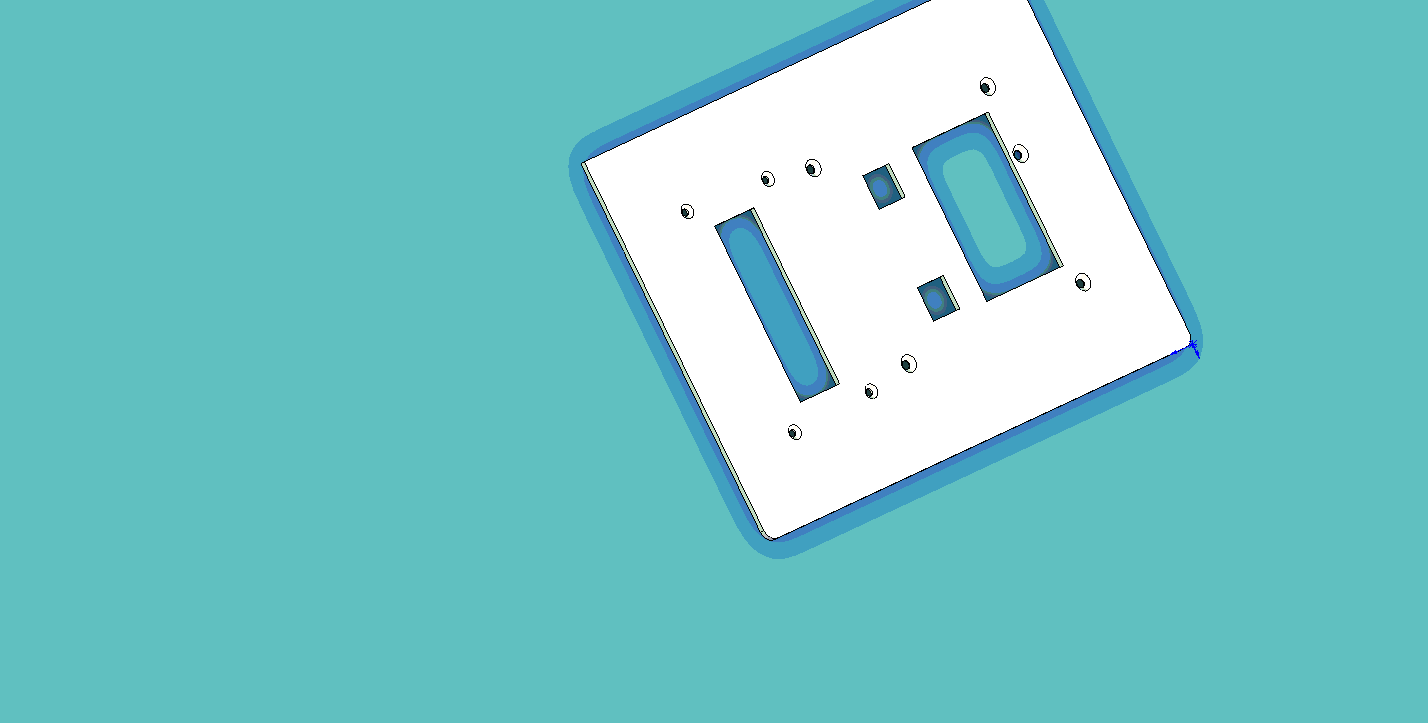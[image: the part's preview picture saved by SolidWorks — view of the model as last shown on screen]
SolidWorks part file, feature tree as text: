
SOLIDWORKS PART (.sldprt)
format: sldprt  version: not decoded by parser v0  size: 308,224 bytes
history: native  units: mm
features: plane x3, chamfer x2, material x1, sketch x1, extrude x1, fillet x1 (+10 scaffold rows collapsed)
feature tree (19):
  scaffold x10  (default folders/planes/origin — collapsed)
  material  "Matériau <non spécifié>"
  plane  "Plan de face"
  plane  "Plan de dessus"
  plane  "Plan de droite"
  sketch  "Esquisse1"  dims[c1.D25=2.5mm c1.D26=3.0mm c1.D1=136.0mm c1.D2=195.0mm c1.D3=140.0mm c1.D4=63.0mm c1.D5=18.0mm c1.D6=36.5mm c1.D7=28.5mm c1.D8=33.0mm c1.D9=30.5mm c1.D10=110.5mm c1.D11=103.0mm c1.D12=42.0mm c1.D13=82.0mm c1.D14=81.5mm c1.D15=12.0mm c1.D16=55.0mm c1.D17=35.0mm c1.D18=40.5mm c1.D19=35.0mm c2.D7=28.5mm c2.D20=30.0mm c2.D21=106.0mm c2.D22=107.5mm c2.D23=165.5mm c2.D24=129.5mm c2.D27=57.0mm]
  extrude  "Extrusion1"  Depth=2mm
  chamfer  "Chanfrein1"  Distance=1.5mm Angle=45deg
  fillet  "Congé1"  Radius=4mm
  chamfer  "Chanfrein2"  Distance=1.25mm Angle=45deg
decode coverage: 5 of 5 modeling features carry decoded parameters
note: suppression state not decoded; provenance and decode notes live in map.json
